# Revit family: SKSMUKabelrinne SKS-Magic® 110 ungelocht FS_FT_110_115_120_130_140_150_160
name_source: partatom
category: Generic Models
revit_build: Autodesk Revit 2017 (Build: 20190508_0315(x64)
units: mm (PartAtom-declared; Revit-internal decimal feet)

## family parameters
Always vertical = Yes
Can host rebar = No
Cut with Voids When Loaded = No
Part Type = Normal
Room Calculation Point = No
Round Connector Dimension = Use Diameter
Shared = No
Work Plane-Based = No

## types (14) — shared parameters
Cut's number = 2
Height = 110 mm  [stored 0.360892 ft]
Length = 3050 mm  [stored 10.0066 ft]
Length 1 = 3000 mm  [stored 9.84252 ft]
Length 2 = 50 mm  [stored 0.164042 ft]
Manufacturer = OBO BETTERMANN
URL = http://www.obo-bettermann.com
Width 2 = 7 mm

## per-type parameters (varying)
| type | GTIN | Manufacturer Art.No. | Material | Width | Width 1 |
| SKSMU 110 FS | 4012195833925 | 6059836 | Strip-galvanised | 100 mm  [stored 0.328084 ft] | 50 mm  [stored 0.164042 ft] |
| SKSMU 115 FS | 4012195833932 | 6059838 | Strip-galvanised | 150 mm | 75 mm |
| SKSMU 120 FS | 4012195833949 | 6059840 | Strip-galvanised | 200 mm  [stored 0.656168 ft] | 100 mm  [stored 0.328084 ft] |
| SKSMU 130 FS | 4012195833987 | 6059842 | Strip-galvanised | 300 mm | 150 mm |
| SKSMU 140 FS | 4012195833994 | 6059844 | Strip-galvanised | 400 mm  [stored 1.31234 ft] | 200 mm  [stored 0.656168 ft] |
| SKSMU 150 FS | 4012195834007 | 6059846 | Strip-galvanised | 500 mm  [stored 1.64042 ft] | 250 mm  [stored 0.82021 ft] |
| SKSMU 160 FS | 4012195834038 | 6059848 | Strip-galvanised | 600 mm | 300 mm |
| SKSMU 110 FT | 4012195834045 | 6059853 | Hot dip galvanised | 100 mm  [stored 0.328084 ft] | 50 mm  [stored 0.164042 ft] |
| SKSMU 115 FT | 4012195834052 | 6059855 | Hot dip galvanised | 150 mm | 75 mm |
| SKSMU 120 FT | 4012195834069 | 6059857 | Hot dip galvanised | 200 mm  [stored 0.656168 ft] | 100 mm  [stored 0.328084 ft] |
| SKSMU 130 FT | 4012195834106 | 6059859 | Hot dip galvanised | 300 mm | 150 mm |
| SKSMU 140 FT | 4012195834113 | 6059861 | Hot dip galvanised | 400 mm  [stored 1.31234 ft] | 200 mm  [stored 0.656168 ft] |
| SKSMU 150 FT | 4012195834120 | 6059863 | Hot dip galvanised | 500 mm  [stored 1.64042 ft] | 250 mm  [stored 0.82021 ft] |
| SKSMU 160 FT | 4012195834151 | 6059865 | Hot dip galvanised | 600 mm | 300 mm |

note: column(s) folded — value = type name in every type: Article Type

note: [stored X ft] marks values corroborated as IEEE doubles in the binary element streams (Revit-internal decimal feet)

## geometry (parser evidence)
native form markers: Sweep x1
no freeform markers — native parametric forms only
